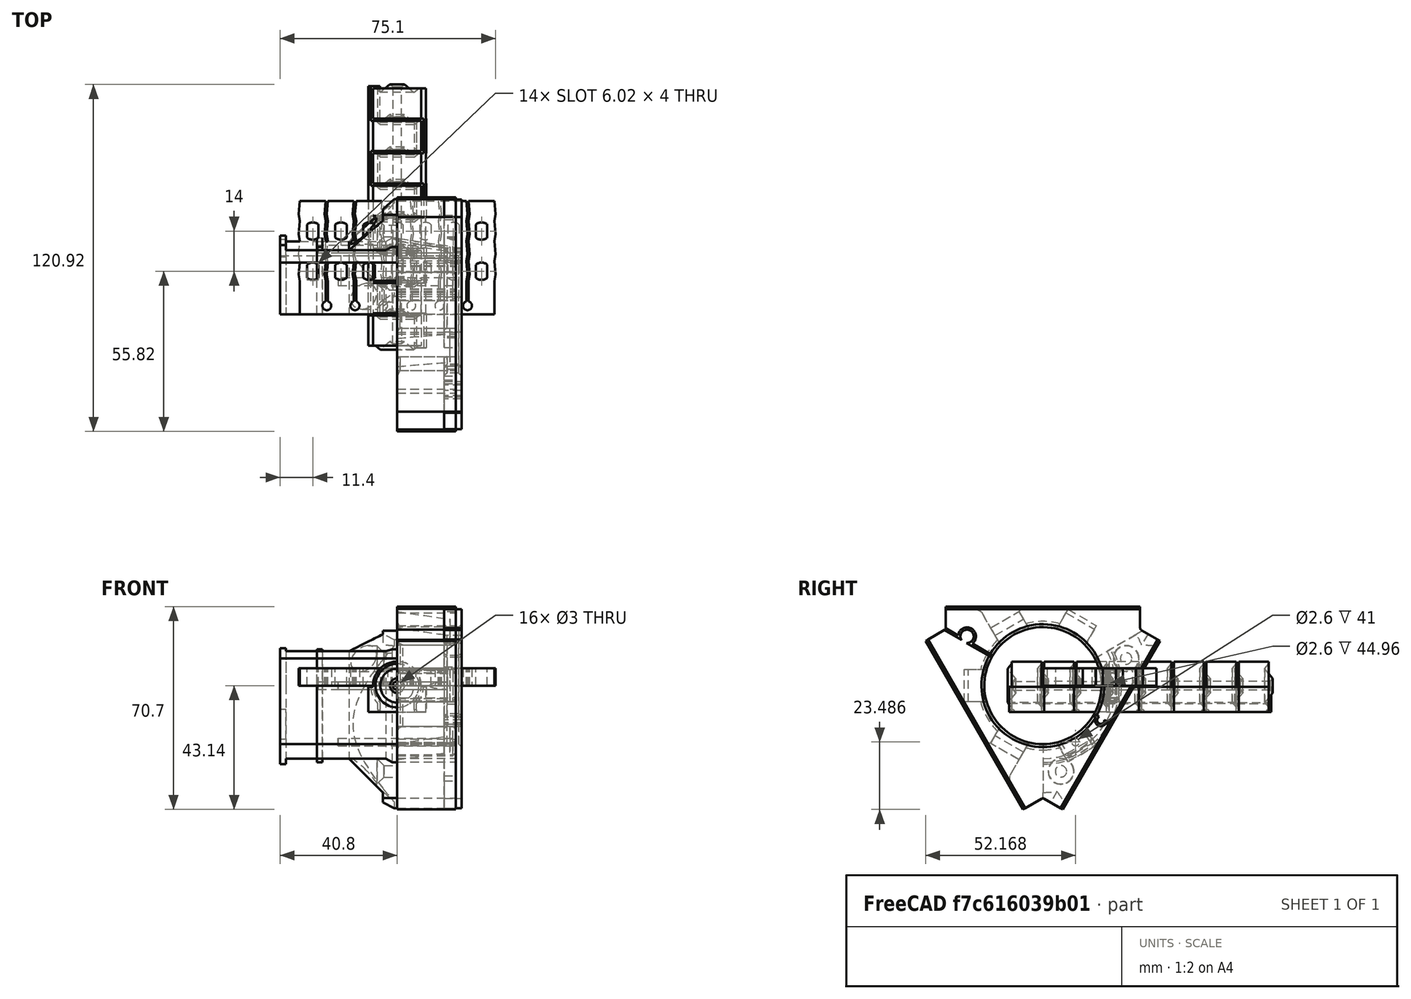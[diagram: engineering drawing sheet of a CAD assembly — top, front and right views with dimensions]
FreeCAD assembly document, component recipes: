
FREECAD ASSEMBLY — COMPONENT RECIPES ("BaseHingeModel_ver1.3_BandOnAxisBander")

This assembly document has 9 components, labeled P0..P8 below (a component is one placed body or linked part). 8 of them carry a construction recipe — the FreeCAD feature program that regenerates the part from scratch, quoted from this document or its linked companion documents; the rest are supplied as boundary geometry only. No exploded tour is included for this assembly.
NOTE — document 2 of 2 of this assembly tour. The two overview renders and the header above are repeated from document 1; the component sections below continue where the previous document stopped.
COMPONENT P8 — recipe-attached ("PetalPart", modeled in this document).
Construction recipe (the document's own serialized feature program — sketch geometry with constraints, then the solid features built on it; lengths are millimeters unless a unit is written):

FEATURE [Sketcher::SketchObject] Sketch029  label="MaxPetalBase"
  FullyConstrained = false
  MapMode = 5
  Placement = pos=(0,0,0) rot=(0.57735,0.57735,0.57735;2.0944rad)
  Support = -> [YZ_Plane015]
  expr: Constraints[0] = Spreadsheet.mmAxisTubeDia + 2 * Spreadsheet.mmFixatorThick
  expr: Constraints[12] = Spreadsheet.mmAxisTubeDia / 2 + Spreadsheet.mmPetalHightMax
  expr: Constraints[16] = Spreadsheet.mmPetalWidth
  expr: Constraints[1] = Spreadsheet.mmAxisTubeDia
  expr: Constraints[6] = Spreadsheet.mmAxisTubeDia + Spreadsheet.mmTwoSideTapeThick * 2
  sketch-geometry (7):
    g0: Circle CenterX=0 CenterY=0 CenterZ=0 NormalX=0 NormalY=0 NormalZ=1 AngleXU=0 Radius=39.8652
    g1: Circle CenterX=0 CenterY=0 CenterZ=0 NormalX=0 NormalY=0 NormalZ=1 AngleXU=0 Radius=26.62
    g2: ArcOfCircle CenterX=0 CenterY=0 CenterZ=0 NormalX=0 NormalY=0 NormalZ=1 AngleXU=0 Radius=20.4 StartAngle=3.89684 EndAngle=6.80091
    g3: LineSegment StartX=19.8084 StartY=5.27991 StartZ=0 EndX=26.52 EndY=5.27991 EndZ=0
    g4: LineSegment StartX=26.52 StartY=5.27991 StartZ=0 EndX=26.52 EndY=-5.27991 EndZ=0
    g5: LineSegment StartX=26.52 StartY=-5.27991 StartZ=0 EndX=19.8084 EndY=-5.27991 EndZ=0
    g6: ArcOfCircle CenterX=0 CenterY=0 CenterZ=0 NormalX=0 NormalY=0 NormalZ=1 AngleXU=0 Radius=20.5 StartAngle=6.02269 EndAngle=6.54368
  constraints (20):
    c: Diameter(g1) = 53.24
    c: Diameter(g2) = 40.8
    c: Coincident(g3,g4)
    c: Coincident(g4,g5)
    c: PointOnObject(g3,g2)
    c: Coincident(g6,g0)
    c: Diameter(g6) = 41
    c: Coincident(g1,g6)
    c: Coincident(g0,g2)
    c: Vertical(g4)
    c: PointOnObject(g3,g6)
    c: PointOnObject(g5,g6)
    c: DistanceX(g-1,g4) = 26.52
    c: Horizontal(g3)
    c: Horizontal(g5)
    c: Symmetric(g5,g3,g-1)
    c: DistanceY(g5,g3) = 10.5598
    c: Coincident(g-1,g6)
    c: PointOnObject(g6,g5)
    c: PointOnObject(g6,g3)
FEATURE [Sketcher::SketchObject] Sketch030  label="MinPetalBase"
  AttachmentOffset = pos=(0,0,20.4) rot=(0,0,1;0rad)
  FullyConstrained = false
  MapMode = 5
  Placement = pos=(20.4,-4.5e-15,4.5e-15) rot=(0.57735,0.57735,0.57735;2.0944rad)
  Support = -> [YZ_Plane015]
  expr: .AttachmentOffset.Base.z = Spreadsheet.mmFixatorHight
  expr: Constraints[0] = Spreadsheet.mmAxisTubeDia + 2 * Spreadsheet.mmFixatorThick
  expr: Constraints[11] = Spreadsheet.mmAxisTubeDia / 2 + Spreadsheet.mmPetalHightMin
  expr: Constraints[15] = Spreadsheet.mmPetalWidth
  expr: Constraints[1] = Spreadsheet.mmAxisTubeDia
  expr: Constraints[5] = Spreadsheet.mmAxisTubeDia + Spreadsheet.mmTwoSideTapeThick * 2
  sketch-geometry (7):
    g0: Circle CenterX=0 CenterY=1.8e-15 CenterZ=0 NormalX=0 NormalY=0 NormalZ=1 AngleXU=0 Radius=39.865
    g1: Circle CenterX=0 CenterY=1.8e-15 CenterZ=0 NormalX=0 NormalY=0 NormalZ=1 AngleXU=0 Radius=26.62
    g2: ArcOfCircle CenterX=0 CenterY=1.8e-15 CenterZ=0 NormalX=0 NormalY=0 NormalZ=1 AngleXU=0 Radius=20.4 StartAngle=3.86544 EndAngle=6.7404
    g3: LineSegment StartX=19.8084 StartY=5.27991 StartZ=0 EndX=23.46 EndY=5.27991 EndZ=0
    g4: LineSegment StartX=23.46 StartY=5.27991 StartZ=0 EndX=23.46 EndY=-5.27991 EndZ=0
    g5: LineSegment StartX=23.46 StartY=-5.27991 StartZ=0 EndX=19.8084 EndY=-5.27991 EndZ=0
    g6: ArcOfCircle CenterX=0 CenterY=1.8e-15 CenterZ=0 NormalX=0 NormalY=0 NormalZ=1 AngleXU=0 Radius=20.5 StartAngle=6.02269 EndAngle=6.54368
  constraints (20):
    c: Diameter(g1) = 53.24
    c: Diameter(g2) = 40.8
    c: Coincident(g3,g4)
    c: Coincident(g4,g5)
    c: Coincident(g6,g0)
    c: Diameter(g6) = 41
    c: Coincident(g1,g6)
    c: Coincident(g0,g2)
    c: Vertical(g4)
    c: PointOnObject(g3,g6)
    c: PointOnObject(g5,g6)
    c: DistanceX(g-1,g4) = 23.46
    c: PointOnObject(g6,g5)
    c: PointOnObject(g6,g3)
    c: Coincident(g6,g-1)
    c: DistanceY(g5,g3) = 10.5598
    c: Symmetric(g5,g3,g-1)
    c: Horizontal(g3)
    c: Horizontal(g5)
    c: PointOnObject(g6,g-2)
FEATURE [PartDesign::AdditiveLoft] AdditiveLoft  label="PetalBodyBodyAdditiveLoft"
  Closed = false
  Placement = pos=(0,0,0) rot=(0.57735,0.57735,0.57735;2.0944rad)
  Profile = -> Sketch029
  Ruled = false
  Sections = -> [Sketch030]
FEATURE [PartDesign::Chamfer] Chamfer
  Angle = 45
  Base = -> AdditiveLoft [Edge8,Edge9,Edge6,Edge3,Edge2,Edge1,Edge11,Edge5]
  BaseFeature = -> AdditiveLoft
  ChamferType = 0
  FlipDirection = false
  Placement = pos=(0,0,0) rot=(0.57735,0.57735,0.57735;2.0944rad)
  Size = 1
  Size2 = 1
  SupportTransform = false
  UseAllEdges = false
FEATURE [PartDesign::Body] Body008  label="PetalBodyPart"
  Group = -> [Sketch029,Sketch030,AdditiveLoft,Chamfer]
  Origin = -> Origin015
  Tip = -> Chamfer
PROVENANCE & LICENSES
A FreeCAD (.FCStd) document from a public repository crawl; recipes are the document's own serialized feature recipes (and, for linked parts, companion documents' recipes).
License: as declared in the source repository (recorded in the dataset sidecar).
